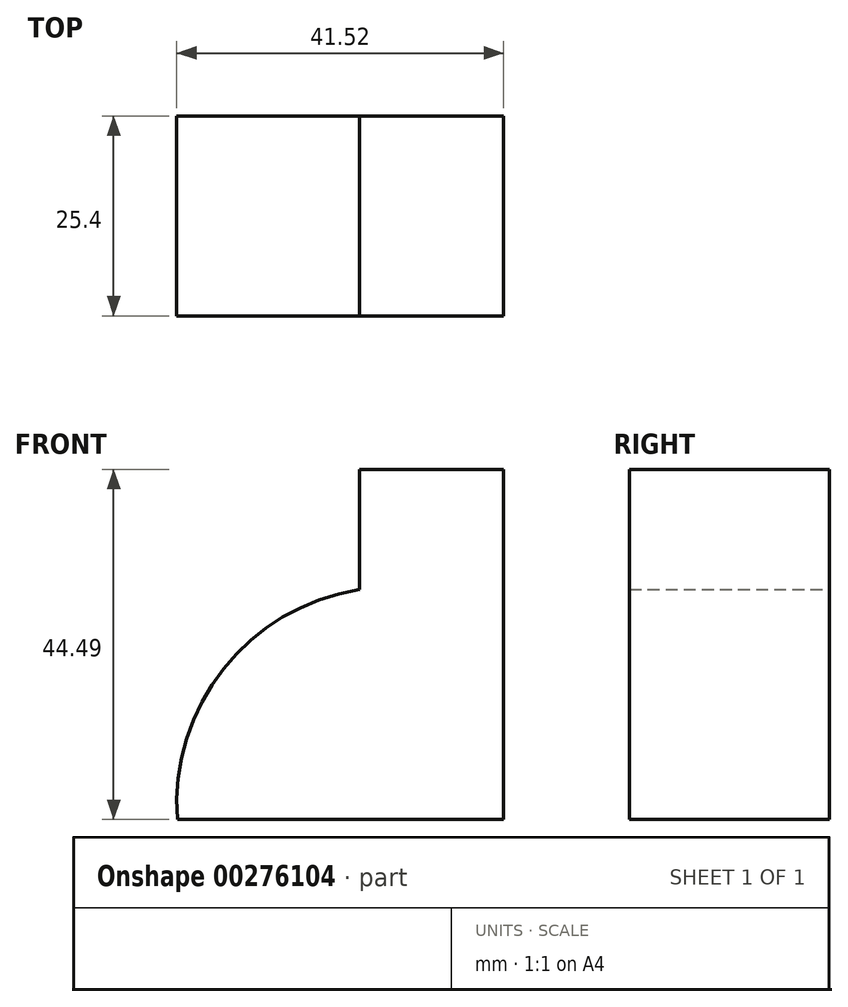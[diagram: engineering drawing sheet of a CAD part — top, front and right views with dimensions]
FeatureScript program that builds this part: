
annotation { "Feature Type Name" : "Feature", "Feature Type Description" : "" }
export const myFeature = defineFeature(function(context is Context, id is Id, definition is map)
    precondition{}
    {
        {
            var Q0;
            Q0=qCreatedBy(makeId("Front.planeOp"),FACE);
            var sketch = newSketch(context, id + "F0", { "sketchPlane" : qUnion([Q0])});
            skLineSegment(sketch, "E0", {"start": v(0, 44.5) * mm, "end": v(0, 0) * mm});
            skLineSegment(sketch, "E1", {"start": v(0, 0) * mm, "end": v(-41.44, 0) * mm});
            skLineSegment(sketch, "E2", {"start": v(-18.33, 29.22) * mm, "end": v(-18.33, 44.5) * mm});
            skLineSegment(sketch, "E3", {"start": v(-18.33, 44.5) * mm, "end": v(0, 44.5) * mm});
            skArc(sketch, "E4", {"start": v(-18.33, 29.22) * mm, "mid": v(-35.6, 19.12) * mm, "end": v(-41.44, 0) * mm});
            skSolve(sketch);
        }
        {
            var Q0;
            Q0 = qSketchRegion(id + "F0", true);
            extrude(context, id + "F1", {"entities" : qUnion([Q0]), "depth" : 25.4 * mm});
        }
    });
